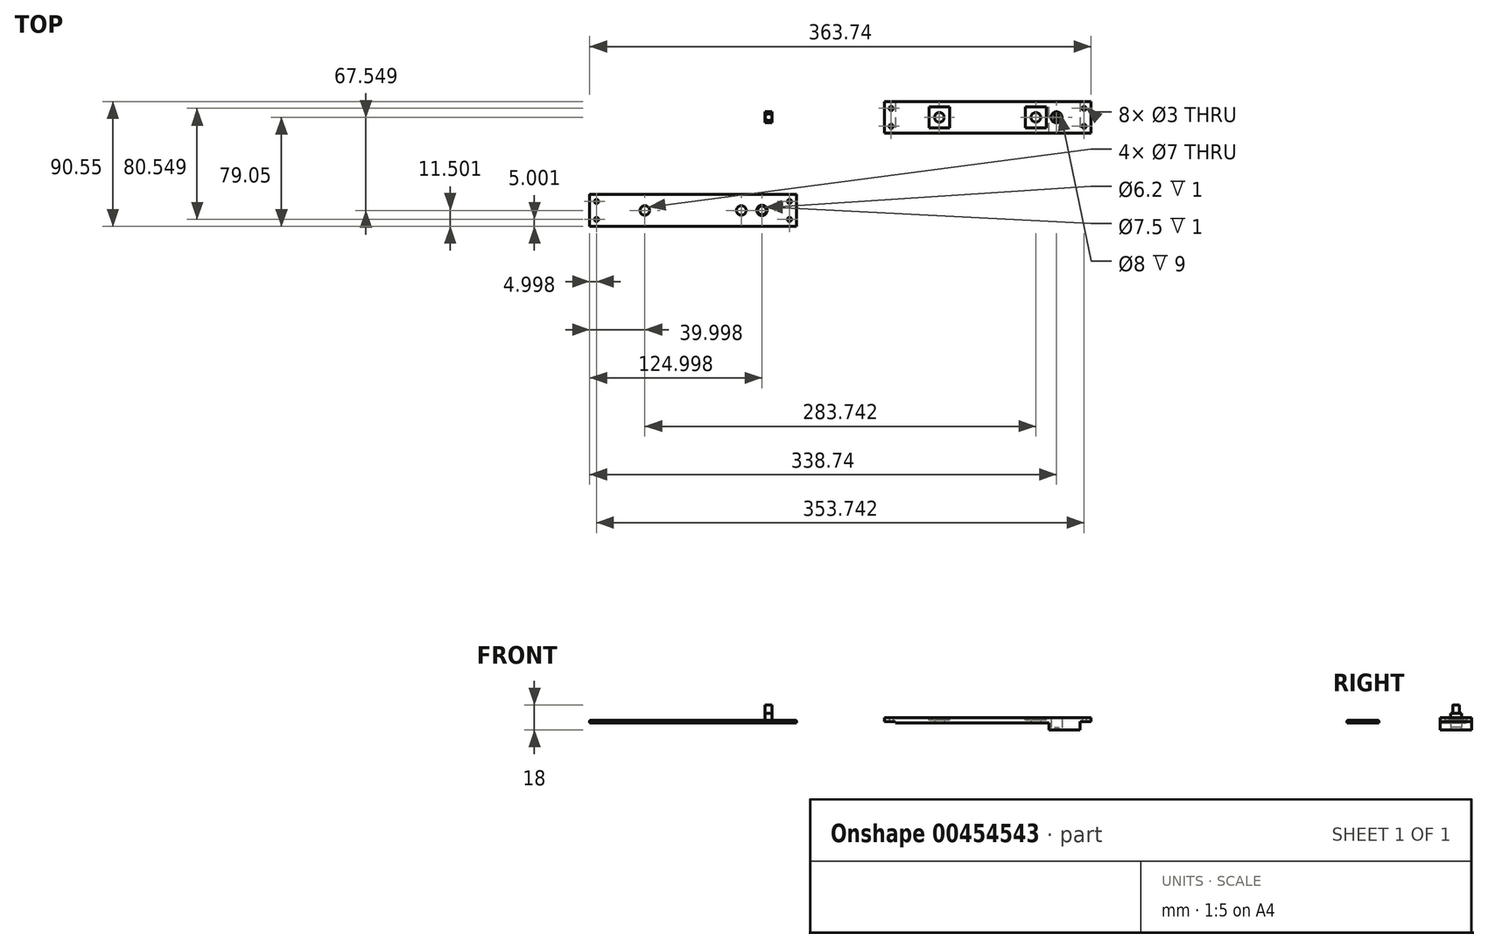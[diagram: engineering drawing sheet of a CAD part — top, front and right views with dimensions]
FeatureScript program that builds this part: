
annotation { "Feature Type Name" : "Feature", "Feature Type Description" : "" }
export const myFeature = defineFeature(function(context is Context, id is Id, definition is map)
    precondition{}
    {
        {
            var Q0;
            Q0=qCreatedBy(makeId("Top.planeOp"),FACE);
            var sketch = newSketch(context, id + "F0", { "sketchPlane" : qUnion([Q0])});
            skLineSegment(sketch, "E0.bottom", {"start": v(75, -11.5) * mm, "end": v(-75, -11.5) * mm});
            skLineSegment(sketch, "E0.top", {"start": v(75, 11.5) * mm, "end": v(-75, 11.5) * mm});
            skLineSegment(sketch, "E0.left", {"start": v(75, -11.5) * mm, "end": v(75, 11.5) * mm});
            skLineSegment(sketch, "E0.right", {"start": v(-75, -11.5) * mm, "end": v(-75, 11.5) * mm});
            skPoint(sketch, "E0.middle", {"position": v(0, 0) * mm});
            skLineSegment(sketch, "E1.bottom", {"start": v(-75, 11.5) * mm, "end": v(-67, 11.5) * mm, "construction": true});
            skLineSegment(sketch, "E1.top", {"start": v(-75, -11.5) * mm, "end": v(-67, -11.5) * mm, "construction": true});
            skLineSegment(sketch, "E1.left", {"start": v(-75, 11.5) * mm, "end": v(-75, -11.5) * mm, "construction": true});
            skLineSegment(sketch, "E1.right", {"start": v(-67, 11.5) * mm, "end": v(-67, -11.5) * mm, "construction": true});
            skLineSegment(sketch, "E2.bottom", {"start": v(75, -11.5) * mm, "end": v(67, -11.5) * mm, "construction": true});
            skLineSegment(sketch, "E2.top", {"start": v(75, 11.5) * mm, "end": v(67, 11.5) * mm, "construction": true});
            skLineSegment(sketch, "E2.left", {"start": v(75, -11.5) * mm, "end": v(75, 11.5) * mm, "construction": true});
            skLineSegment(sketch, "E2.right", {"start": v(67, -11.5) * mm, "end": v(67, 11.5) * mm, "construction": true});
            skCircle(sketch, "E3", {"center": v(-35, 0) * mm, "radius": 3.5 * mm});
            skCircle(sketch, "E4", {"center": v(35, 0) * mm, "radius": 3.5 * mm});
            skCircle(sketch, "E5", {"center": v(50, 0) * mm, "radius": 4 * mm});
            skLineSegment(sketch, "E6.left", {"start": v(51.5, -3.7) * mm, "end": v(51.5, 3.7) * mm, "construction": true});
            skLineSegment(sketch, "E6.right", {"start": v(48.5, -3.7) * mm, "end": v(48.5, 3.7) * mm, "construction": true});
            skCircle(sketch, "E7", {"center": v(-70, 6.5) * mm, "radius": 1.5 * mm});
            skCircle(sketch, "E8", {"center": v(-70, -6.5) * mm, "radius": 1.5 * mm});
            skCircle(sketch, "E9", {"center": v(70, 6.5) * mm, "radius": 1.5 * mm});
            skCircle(sketch, "E10", {"center": v(70, -6.5) * mm, "radius": 1.5 * mm});
            skSolve(sketch);
        }
        {
            var Q0;
            Q0=qCreatedBy(makeId("Top.planeOp"),FACE);
            var sketch = newSketch(context, id + "F1", { "sketchPlane" : qUnion([Q0])});
            skLineSegment(sketch, "E11.bottom", {"start": v(-156.38, -3.9) * mm, "end": v(-161.38, -3.9) * mm});
            skLineSegment(sketch, "E11.top", {"start": v(-156.38, 4.1) * mm, "end": v(-161.38, 4.1) * mm});
            skLineSegment(sketch, "E11.left", {"start": v(-156.38, -3.9) * mm, "end": v(-156.38, 4.1) * mm});
            skLineSegment(sketch, "E11.right", {"start": v(-161.38, -3.9) * mm, "end": v(-161.38, 4.1) * mm});
            skPoint(sketch, "E11.middle", {"position": v(-158.88, 0.1) * mm});
            skSolve(sketch);
        }
        {
            var Q0;
            Q0=makeQuery(id+"F1.imprint","IMPRINT",FACE,{"disambiguationData":[TD([[makeQuery(id+"F1.imprint","IMPRINT",EDGE,{"derivedFrom":sQuery(id+"F1.wireOp",EDGE,"E11.bottom")}),-1.0]])]});
            extrude(context, id + "F2", {"entities" : qUnion([Q0]), "depth" : 7 * mm});
        }
        {
            var Q0;
            Q0=makeQuery(id+"F2.opExtrude","CAP_FACE",FACE,{"disambiguationData":[OSD([sQuery(id+"F1.wireOp",EDGE,"E11.bottom"),sQuery(id+"F1.wireOp",EDGE,"E11.top"),sQuery(id+"F1.wireOp",EDGE,"E11.left"),sQuery(id+"F1.wireOp",EDGE,"E11.right")])],"isStart":false});
            var sketch = newSketch(context, id + "F3", { "sketchPlane" : qUnion([Q0])});
            skCircle(sketch, "E12", {"center": v(-158.88, 0.1) * mm, "radius": 2.5 * mm});
            skPoint(sketch, "E12.centerSnap0", {"position": v(-161.38, 0.1) * mm});
            skPoint(sketch, "E12.centerSnap1", {"position": v(-158.88, 4.1) * mm});
            skSolve(sketch);
        }
        {
            var Q0;
            {var subQ0=sQuery(id+"F3.wireOp",EDGE,"E12");var subQ1=makeQuery(id+"F3.imprint","INTERSECT",VERTEX,{"derivedFrom":[makeQuery(id+"F2.opExtrude","CAP_EDGE",EDGE,{"disambiguationData":[OSD([sQuery(id+"F1.wireOp",EDGE,"E11.left")])],"isStart":false}),subQ0]});Q0=makeQuery(id+"F3.imprint","IMPRINT",FACE,{"disambiguationData":[TD([[makeQuery(id+"F3.imprint","IMPRINT",EDGE,{"disambiguationData":[TD([[subQ1,-1.0]])],"derivedFrom":subQ0}),1.0]])]});}
            extrude(context, id + "F4", {"entities" : qUnion([Q0]), "operationType" : NewBodyOperationType.ADD, "depth" : 6 * mm});
        }
        {
            var Q0;
            Q0=makeQuery(id+"F0.imprint","IMPRINT",FACE,{"disambiguationData":[TD([[makeQuery(id+"F0.imprint","IMPRINT",EDGE,{"derivedFrom":sQuery(id+"F0.wireOp",EDGE,"E0.bottom")}),-1.0]])]});
            var Q1;
            {var subQ0=sQuery(id+"F0.wireOp",EDGE,"E6.left");Q1=makeQuery(id+"F0.imprint","IMPRINT",FACE,{"disambiguationData":[TD([[makeQuery(id+"F0.imprint","IMPRINT",EDGE,{"derivedFrom":subQ0}),1.0]])]});}
            extrude(context, id + "F5", {"entities" : qUnion([Q0, Q1]), "depth" : 4 * mm});
        }
        {
            var Q0;
            Q0=qCreatedBy(makeId("Top.planeOp"),FACE);
            var sketch = newSketch(context, id + "F6", { "sketchPlane" : qUnion([Q0])});
            skLineSegment(sketch, "E13.bottom", {"start": v(-138.74, -79.05) * mm, "end": v(-288.74, -79.05) * mm});
            skLineSegment(sketch, "E13.top", {"start": v(-138.74, -56.05) * mm, "end": v(-288.74, -56.05) * mm});
            skLineSegment(sketch, "E13.left", {"start": v(-138.74, -79.05) * mm, "end": v(-138.74, -56.05) * mm});
            skLineSegment(sketch, "E13.right", {"start": v(-288.74, -79.05) * mm, "end": v(-288.74, -56.05) * mm});
            skPoint(sketch, "E13.middle", {"position": v(-213.74, -67.55) * mm});
            skLineSegment(sketch, "E14.bottom", {"start": v(-288.74, -56.05) * mm, "end": v(-280.74, -56.05) * mm, "construction": true});
            skLineSegment(sketch, "E14.top", {"start": v(-288.74, -79.05) * mm, "end": v(-280.74, -79.05) * mm, "construction": true});
            skLineSegment(sketch, "E14.left", {"start": v(-288.74, -56.05) * mm, "end": v(-288.74, -79.05) * mm, "construction": true});
            skLineSegment(sketch, "E14.right", {"start": v(-280.74, -56.05) * mm, "end": v(-280.74, -79.05) * mm, "construction": true});
            skLineSegment(sketch, "E15.bottom", {"start": v(-138.74, -79.05) * mm, "end": v(-146.74, -79.05) * mm, "construction": true});
            skLineSegment(sketch, "E15.top", {"start": v(-138.74, -56.05) * mm, "end": v(-146.74, -56.05) * mm, "construction": true});
            skLineSegment(sketch, "E15.left", {"start": v(-138.74, -79.05) * mm, "end": v(-138.74, -56.05) * mm, "construction": true});
            skLineSegment(sketch, "E15.right", {"start": v(-146.74, -79.05) * mm, "end": v(-146.74, -56.05) * mm, "construction": true});
            skCircle(sketch, "E16", {"center": v(-248.74, -67.55) * mm, "radius": 3.5 * mm});
            skCircle(sketch, "E17", {"center": v(-178.74, -67.55) * mm, "radius": 3.5 * mm});
            skCircle(sketch, "E18", {"center": v(-163.74, -67.55) * mm, "radius": 3.1 * mm});
            skCircle(sketch, "E19", {"center": v(-283.74, -61.05) * mm, "radius": 1.5 * mm});
            skCircle(sketch, "E20", {"center": v(-283.74, -74.05) * mm, "radius": 1.5 * mm});
            skCircle(sketch, "E21", {"center": v(-143.74, -61.05) * mm, "radius": 1.5 * mm});
            skCircle(sketch, "E22", {"center": v(-143.74, -74.05) * mm, "radius": 1.5 * mm});
            skSolve(sketch);
        }
        {
            var Q0;
            Q0=makeQuery(id+"F6.imprint","IMPRINT",FACE,{"disambiguationData":[TD([[makeQuery(id+"F6.imprint","IMPRINT",EDGE,{"derivedFrom":sQuery(id+"F6.wireOp",EDGE,"E13.bottom")}),-1.0]])]});
            extrude(context, id + "F7", {"entities" : qUnion([Q0]), "depth" : 2 * mm});
        }
        {
            var Q0;
            Q0=makeQuery(id+"F7.opExtrude","CAP_FACE",FACE,{"disambiguationData":[OSD([sQuery(id+"F6.wireOp",EDGE,"E13.bottom"),sQuery(id+"F6.wireOp",EDGE,"E13.top"),sQuery(id+"F6.wireOp",EDGE,"E13.left"),sQuery(id+"F6.wireOp",EDGE,"E13.right"),sQuery(id+"F6.wireOp",EDGE,"E16"),sQuery(id+"F6.wireOp",EDGE,"E17"),sQuery(id+"F6.wireOp",EDGE,"E18")])],"isStart":false});
            var sketch = newSketch(context, id + "F8", { "sketchPlane" : qUnion([Q0])});
            skCircle(sketch, "E23", {"center": v(-163.74, -67.55) * mm, "radius": 3.75 * mm});
            skSolve(sketch);
        }
        {
            var Q0;
            Q0 = qSketchRegion(id + "F8", true);
            extrude(context, id + "F9", {"entities" : qUnion([Q0]), "operationType" : NewBodyOperationType.REMOVE, "oppositeDirection" : true, "depth" : 1 * mm});
        }
        {
            var Q0;
            Q0=makeQuery(id+"F5.opExtrude","SWEPT_FACE",FACE,{"disambiguationData":[OSD([sQuery(id+"F0.wireOp",EDGE,"E0.bottom")])]});
            var sketch = newSketch(context, id + "F10", { "sketchPlane" : qUnion([Q0])});
            skLineSegment(sketch, "E24.bottom", {"start": v(-75, 0) * mm, "end": v(-67, 0) * mm});
            skLineSegment(sketch, "E24.top", {"start": v(-75, 1) * mm, "end": v(-67, 1) * mm});
            skLineSegment(sketch, "E24.left", {"start": v(-75, 0) * mm, "end": v(-75, 1) * mm});
            skLineSegment(sketch, "E24.right", {"start": v(-67, 0) * mm, "end": v(-67, 1) * mm});
            skLineSegment(sketch, "E25.bottom", {"start": v(75, 0) * mm, "end": v(67, 0) * mm});
            skLineSegment(sketch, "E25.top", {"start": v(75, 1) * mm, "end": v(67, 1) * mm});
            skLineSegment(sketch, "E25.left", {"start": v(75, 0) * mm, "end": v(75, 1) * mm});
            skLineSegment(sketch, "E25.right", {"start": v(67, 0) * mm, "end": v(67, 1) * mm});
            skSolve(sketch);
        }
        {
            var Q0;
            Q0 = qSketchRegion(id + "F10", true);
            extrude(context, id + "F11", {"entities" : qUnion([Q0]), "operationType" : NewBodyOperationType.REMOVE, "oppositeDirection" : true, "depth" : 30 * mm});
        }
        {
            var Q0;
            Q0=makeQuery(id+"F5.opExtrude","CAP_FACE",FACE,{"disambiguationData":[OSD([sQuery(id+"F0.wireOp",EDGE,"E0.bottom"),sQuery(id+"F0.wireOp",EDGE,"E0.top"),sQuery(id+"F0.wireOp",EDGE,"E0.left"),sQuery(id+"F0.wireOp",EDGE,"E0.right"),sQuery(id+"F0.wireOp",EDGE,"E3"),sQuery(id+"F0.wireOp",EDGE,"E4"),sQuery(id+"F0.wireOp",EDGE,"E5")])],"isStart":false});
            var sketch = newSketch(context, id + "F12", { "sketchPlane" : qUnion([Q0])});
            skLineSegment(sketch, "E26.bottom", {"start": v(-27.5, -7.5) * mm, "end": v(-42.5, -7.5) * mm});
            skLineSegment(sketch, "E26.top", {"start": v(-27.5, 7.5) * mm, "end": v(-42.5, 7.5) * mm});
            skLineSegment(sketch, "E26.left", {"start": v(-27.5, -7.5) * mm, "end": v(-27.5, 7.5) * mm});
            skLineSegment(sketch, "E26.right", {"start": v(-42.5, -7.5) * mm, "end": v(-42.5, 7.5) * mm});
            skPoint(sketch, "E26.middle", {"position": v(-35, 0) * mm});
            skLineSegment(sketch, "E27.bottom", {"start": v(42.5, -7.5) * mm, "end": v(27.5, -7.5) * mm});
            skLineSegment(sketch, "E27.top", {"start": v(42.5, 7.5) * mm, "end": v(27.5, 7.5) * mm});
            skLineSegment(sketch, "E27.left", {"start": v(42.5, -7.5) * mm, "end": v(42.5, 7.5) * mm});
            skLineSegment(sketch, "E27.right", {"start": v(27.5, -7.5) * mm, "end": v(27.5, 7.5) * mm});
            skPoint(sketch, "E27.middle", {"position": v(35, 0) * mm});
            skSolve(sketch);
        }
        {
            var Q0;
            Q0=makeQuery(id+"F12.imprint","IMPRINT",FACE,{"disambiguationData":[TD([[makeQuery(id+"F12.imprint","IMPRINT",EDGE,{"derivedFrom":sQuery(id+"F12.wireOp",EDGE,"E26.bottom")}),-1.0]])]});
            var Q1;
            Q1=makeQuery(id+"F12.imprint","IMPRINT",FACE,{"disambiguationData":[TD([[makeQuery(id+"F12.imprint","IMPRINT",EDGE,{"derivedFrom":sQuery(id+"F12.wireOp",EDGE,"E27.bottom")}),-1.0]])]});
            extrude(context, id + "F13", {"entities" : qUnion([Q0, Q1]), "operationType" : NewBodyOperationType.REMOVE, "oppositeDirection" : true, "depth" : 2 * mm});
        }
        {
            var Q0;
            Q0=makeQuery(id+"F5.opExtrude","CAP_FACE",FACE,{"disambiguationData":[OSD([sQuery(id+"F0.wireOp",EDGE,"E0.bottom"),sQuery(id+"F0.wireOp",EDGE,"E0.top"),sQuery(id+"F0.wireOp",EDGE,"E0.left"),sQuery(id+"F0.wireOp",EDGE,"E0.right"),sQuery(id+"F0.wireOp",EDGE,"E3"),sQuery(id+"F0.wireOp",EDGE,"E4"),sQuery(id+"F0.wireOp",EDGE,"E5"),sQuery(id+"F0.wireOp",EDGE,"E6.left"),sQuery(id+"F0.wireOp",EDGE,"E6.right")])],"isStart":false});
            var sketch = newSketch(context, id + "F14", { "sketchPlane" : qUnion([Q0])});
            skCircle(sketch, "E28", {"center": v(50, 0) * mm, "radius": 4 * mm});
            skSolve(sketch);
        }
        {
            var Q0;
            Q0 = qSketchRegion(id + "F14", true);
            extrude(context, id + "F15", {"entities" : qUnion([Q0]), "operationType" : NewBodyOperationType.REMOVE, "oppositeDirection" : true, "depth" : 3 * mm});
        }
        {
            var Q0;
            Q0=makeQuery(id+"F0.imprint","IMPRINT",FACE,{"disambiguationData":[TD([[makeQuery(id+"F0.imprint","IMPRINT",EDGE,{"derivedFrom":sQuery(id+"F0.wireOp",EDGE,"E0.bottom")}),-1.0]])]});
            var sketch = newSketch(context, id + "F16", { "sketchPlane" : qUnion([Q0])});
            skPoint(sketch, "E29.0", {"position": v(67, -11.5) * mm});
            skPoint(sketch, "E29.1", {"position": v(67, 11.5) * mm});
            skLineSegment(sketch, "E30.bottom", {"start": v(67, -11.5) * mm, "end": v(44.5, -11.5) * mm});
            skLineSegment(sketch, "E30.top", {"start": v(67, 11.5) * mm, "end": v(44.5, 11.5) * mm});
            skLineSegment(sketch, "E30.left", {"start": v(67, -11.5) * mm, "end": v(67, 11.5) * mm});
            skLineSegment(sketch, "E30.right", {"start": v(44.5, -11.5) * mm, "end": v(44.5, 11.5) * mm});
            skCircle(sketch, "E31", {"center": v(50, 0) * mm, "radius": 4 * mm});
            skSolve(sketch);
        }
        {
            var Q0;
            Q0=makeQuery(id+"F7.opExtrude","CAP_EDGE",EDGE,{"disambiguationData":[OSD([sQuery(id+"F6.wireOp",EDGE,"E13.right")])],"isStart":false});
            var Q1;
            Q1=makeQuery(id+"F7.opExtrude","CAP_EDGE",EDGE,{"disambiguationData":[OSD([sQuery(id+"F6.wireOp",EDGE,"E13.top")])],"isStart":false});
            var Q2;
            Q2=makeQuery(id+"F7.opExtrude","CAP_EDGE",EDGE,{"disambiguationData":[OSD([sQuery(id+"F6.wireOp",EDGE,"E13.bottom")])],"isStart":false});
            var Q3;
            Q3=makeQuery(id+"F7.opExtrude","CAP_EDGE",EDGE,{"disambiguationData":[OSD([sQuery(id+"F6.wireOp",EDGE,"E13.left")])],"isStart":false});
            fillet(context, id + "F17", {"entities" : qUnion([Q0, Q1, Q2, Q3]), "radius" : 0.5 * mm, "tangentPropagation" : true, "allowEdgeOverflow" : false});
        }
        {
            var Q0;
            Q0 = qSketchRegion(id + "F16", true);
            extrude(context, id + "F18", {"entities" : qUnion([Q0]), "operationType" : NewBodyOperationType.ADD, "oppositeDirection" : true, "depth" : 5 * mm, "offsetDistance" : 25 * mm});
        }
        {
            var Q0;
            Q0=makeQuery(id+"F18.opExtrude","CAP_FACE",FACE,{"disambiguationData":[OSD([sQuery(id+"F16.wireOp",EDGE,"E30.bottom"),sQuery(id+"F16.wireOp",EDGE,"E30.top"),sQuery(id+"F16.wireOp",EDGE,"E30.left"),sQuery(id+"F16.wireOp",EDGE,"E30.right"),sQuery(id+"F16.wireOp",EDGE,"E31")])],"isStart":false});
            var sketch = newSketch(context, id + "F19", { "sketchPlane" : qUnion([Q0])});
            skPoint(sketch, "E32.0", {"position": v(50, 0) * mm});
            skLineSegment(sketch, "E33.bottom", {"start": v(51.5, -3.7) * mm, "end": v(48.5, -3.7) * mm});
            skLineSegment(sketch, "E33.top", {"start": v(51.5, 3.7) * mm, "end": v(48.5, 3.7) * mm});
            skLineSegment(sketch, "E33.left", {"start": v(51.5, -3.7) * mm, "end": v(51.5, 3.7) * mm});
            skLineSegment(sketch, "E33.right", {"start": v(48.5, -3.7) * mm, "end": v(48.5, 3.7) * mm});
            skSolve(sketch);
        }
        {
            var Q0;
            Q0=makeQuery(id+"F19.imprint","IMPRINT",FACE,{"disambiguationData":[TD([[makeQuery(id+"F19.imprint","IMPRINT",EDGE,{"derivedFrom":sQuery(id+"F19.wireOp",EDGE,"E33.bottom")}),-1.0]])]});
            var Q1;
            {var subQ0=sQuery(id+"F19.wireOp",EDGE,"E33.top");Q1=makeQuery(id+"F19.imprint","IMPRINT",FACE,{"disambiguationData":[TD([[makeQuery(id+"F19.imprint","IMPRINT",EDGE,{"derivedFrom":subQ0}),-1.0]])]});}
            var Q2;
            {var subQ0=sQuery(id+"F19.wireOp",EDGE,"E33.bottom");Q2=makeQuery(id+"F19.imprint","IMPRINT",FACE,{"disambiguationData":[TD([[makeQuery(id+"F19.imprint","IMPRINT",EDGE,{"derivedFrom":subQ0}),1.0]])]});}
            extrude(context, id + "F20", {"entities" : qUnion([Q0, Q1, Q2]), "operationType" : NewBodyOperationType.ADD, "oppositeDirection" : true, "depth" : 2 * mm, "offsetDistance" : 25 * mm});
        }
    });
